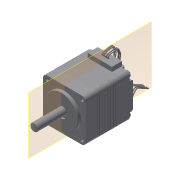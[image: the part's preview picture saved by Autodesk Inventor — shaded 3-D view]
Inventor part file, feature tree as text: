
AUTODESK INVENTOR PART (.ipt)
format: ipt  version: 2019.4 (Build 234330000, 330)  size: 3,369,472 bytes
history: native  units: mm
features: other x8, plane x1
ambient origin geometry x8: Origin, YZ Plane, XZ Plane, XY Plane, X Axis, Y Axis, Z Axis, Center Point
bodies: Solid1 (feature_tree), Solid2 (feature_tree), Solid3 (feature_tree), Solid4 (feature_tree), Solid5 (feature_tree), Solid6 (feature_tree), Solid7 (feature_tree), Solid8 (feature_tree)
feature tree (9):
  plane  "Work Plane1"
  other  "Lagerschild_11_1:1"
  other  "Welle_11_2:1"
  other  "Kollektorschild_11_3:1"
  other  "Schraube_M2x25_4:1"
  other  "Schraube_M2x25_5:1"
  other  "Schraube_M2x25_6:1"
  other  "Schraube_M2x25_7:1"
  other  "Stator_11_8:1"
